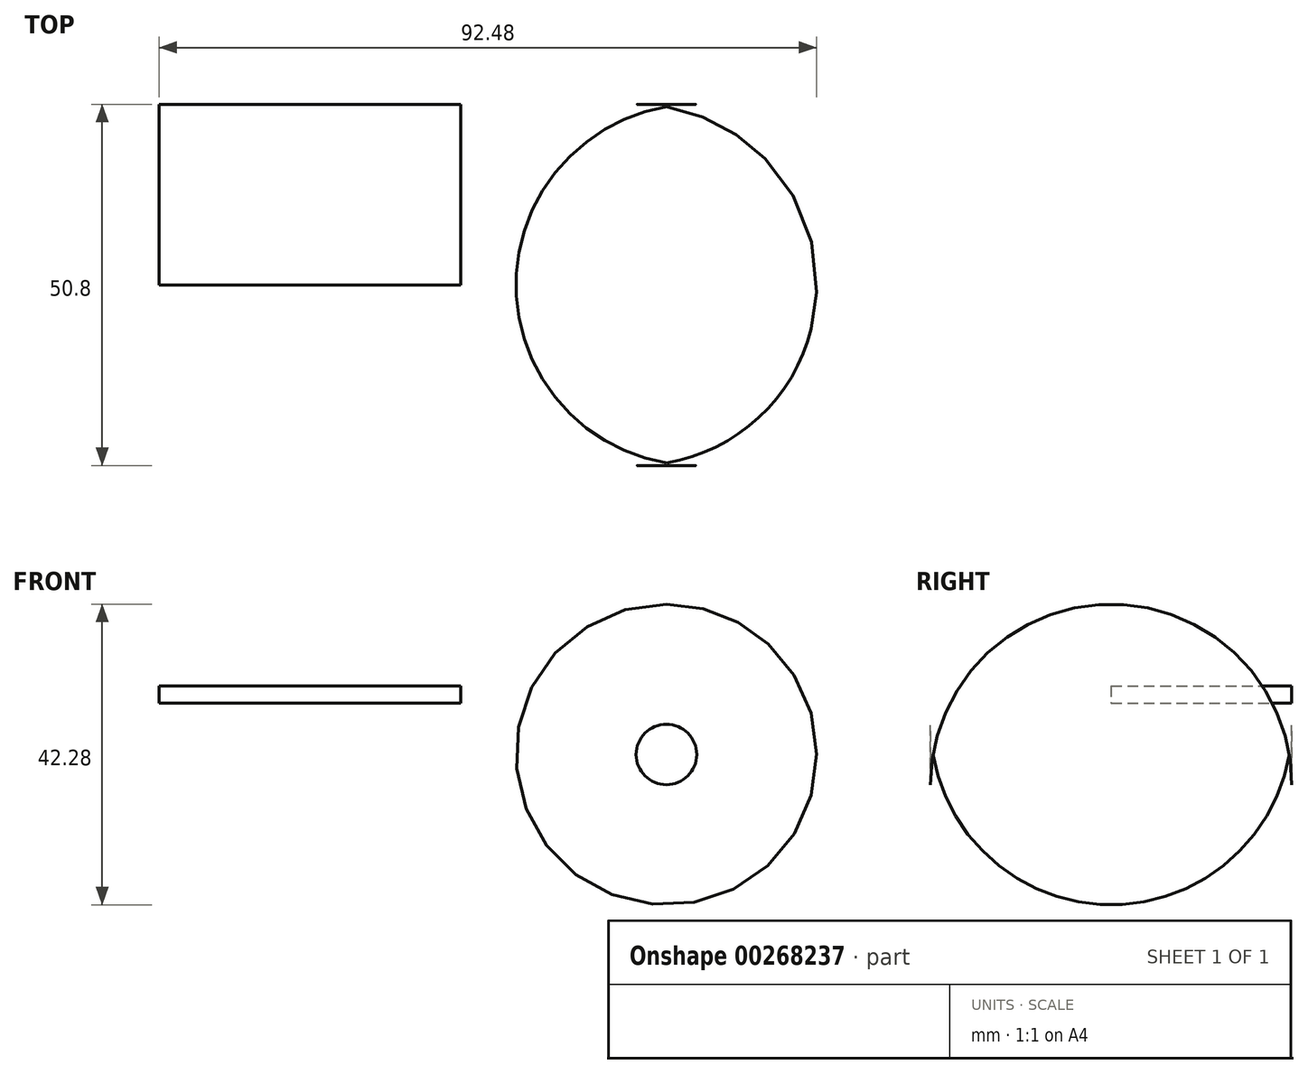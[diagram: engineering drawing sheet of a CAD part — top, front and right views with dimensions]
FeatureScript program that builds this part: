
annotation { "Feature Type Name" : "Feature", "Feature Type Description" : "" }
export const myFeature = defineFeature(function(context is Context, id is Id, definition is map)
    precondition{}
    {
        {
            var Q0;
            Q0=qCreatedBy(makeId("Front.planeOp"),FACE);
            var sketch = newSketch(context, id + "F0", { "sketchPlane" : qUnion([Q0])});
            skCircle(sketch, "E0", {"center": v(-22.41, 11.8) * mm, "radius": 29.66 * mm});
            skSolve(sketch);
        }
        {
            var Q0;
            Q0 = qSketchRegion(id + "F0", true);
            extrude(context, id + "F1", {"entities" : qUnion([Q0]), "depth" : 50.8 * mm});
        }
        {
            var Q0;
            Q0=makeQuery(id+"F1.opExtrude","CAP_FACE",FACE,{"disambiguationData":[OSD([sQuery(id+"F0.wireOp",EDGE,"E0")])],"isStart":false});
            var Q1;
            Q1=makeQuery(id+"F1.opExtrude","CAP_FACE",FACE,{"disambiguationData":[OSD([sQuery(id+"F0.wireOp",EDGE,"E0")])],"isStart":true});
            fillet(context, id + "F2", {"entities" : qUnion([Q0, Q1]), "radius" : 25.4 * mm, "tangentPropagation" : true, "allowEdgeOverflow" : false});
        }
        {
            var Q0;
            Q0=qCreatedBy(makeId("Front.planeOp"),FACE);
            var sketch = newSketch(context, id + "F3", { "sketchPlane" : qUnion([Q0])});
            skLineSegment(sketch, "E1", {"start": v(-26.03, 10.36) * mm, "end": v(-26.03, 2.9) * mm});
            skLineSegment(sketch, "E2", {"start": v(-23.14, 6.63) * mm, "end": v(-23.14, 0) * mm});
            skPoint(sketch, "E2.startSnap0", {"position": v(-26.03, 6.63) * mm});
            skLineSegment(sketch, "E3", {"start": v(-20.73, 6.5) * mm, "end": v(-20.73, 0) * mm});
            skLineSegment(sketch, "E4", {"start": v(-19.04, 6.5) * mm, "end": v(-12.3, 0) * mm});
            skLineSegment(sketch, "E5", {"start": v(-18.07, 9.16) * mm, "end": v(-8.68, 9.16) * mm});
            skEllipse(sketch, "E6", {"center": v(-40, 20.97) * mm, "majorRadius": 9.71 * mm, "minorRadius": 3.12 * mm, "majorAxis": v(0.7, 0.72)});
            skEllipse(sketch, "E7", {"center": v(-11.57, 20) * mm, "majorRadius": 10.03 * mm, "minorRadius": 4.94 * mm, "majorAxis": v(0.91, -0.4)});
            skCircle(sketch, "E8", {"center": v(-25.55, -7.23) * mm, "radius": 7.03 * mm});
            skLineSegment(sketch, "E9.bottom", {"start": v(-31.57, 40.49) * mm, "end": v(-75.91, 40.49) * mm});
            skLineSegment(sketch, "E9.top", {"start": v(-31.57, 38.32) * mm, "end": v(-75.91, 38.32) * mm});
            skLineSegment(sketch, "E9.left", {"start": v(-31.57, 40.49) * mm, "end": v(-31.57, 38.32) * mm});
            skLineSegment(sketch, "E9.right", {"start": v(-75.91, 40.49) * mm, "end": v(-75.91, 38.32) * mm});
            skLineSegment(sketch, "E10.bottom", {"start": v(-41.93, 34.7) * mm, "end": v(-81.94, 34.7) * mm});
            skLineSegment(sketch, "E10.top", {"start": v(-41.93, 32.05) * mm, "end": v(-81.94, 32.05) * mm});
            skLineSegment(sketch, "E10.left", {"start": v(-41.93, 34.7) * mm, "end": v(-41.93, 32.05) * mm});
            skLineSegment(sketch, "E10.right", {"start": v(-81.94, 34.7) * mm, "end": v(-81.94, 32.05) * mm});
            skLineSegment(sketch, "E11.bottom", {"start": v(-48.68, 27.96) * mm, "end": v(-87.96, 27.96) * mm});
            skLineSegment(sketch, "E11.top", {"start": v(-48.68, 25.3) * mm, "end": v(-87.96, 25.3) * mm});
            skLineSegment(sketch, "E11.left", {"start": v(-48.68, 27.96) * mm, "end": v(-48.68, 25.3) * mm});
            skLineSegment(sketch, "E11.right", {"start": v(-87.96, 27.96) * mm, "end": v(-87.96, 25.3) * mm});
            skLineSegment(sketch, "E12.bottom", {"start": v(-51.33, 21.45) * mm, "end": v(-93.75, 21.45) * mm});
            skLineSegment(sketch, "E12.top", {"start": v(-51.33, 19.04) * mm, "end": v(-93.75, 19.04) * mm});
            skLineSegment(sketch, "E12.left", {"start": v(-51.33, 21.45) * mm, "end": v(-51.33, 19.04) * mm});
            skLineSegment(sketch, "E12.right", {"start": v(-93.75, 21.45) * mm, "end": v(-93.75, 19.04) * mm});
            skSolve(sketch);
        }
        {
            var Q0;
            Q0 = qSketchRegion(id + "F3", true);
            var Q1;
            Q1=sQuery(id+"F3.wireOp",EDGE,"E8");
            var Q2;
            Q2=sQuery(id+"F3.wireOp",EDGE,"E7");
            var Q3;
            Q3=sQuery(id+"F3.wireOp",EDGE,"E6");
            extrude(context, id + "F4", {"entities" : qUnion([Q0]), "bodyType" : ToolBodyType.SURFACE, "surfaceEntities" : qUnion([Q1, Q2, Q3]), "depth" : 25.4 * mm});
        }
        {
            var Q0;
            Q0 = qSketchRegion(id + "F3", true);
            extrude(context, id + "F5", {"entities" : qUnion([Q0]), "operationType" : NewBodyOperationType.ADD, "depth" : 25.4 * mm});
        }
    });
